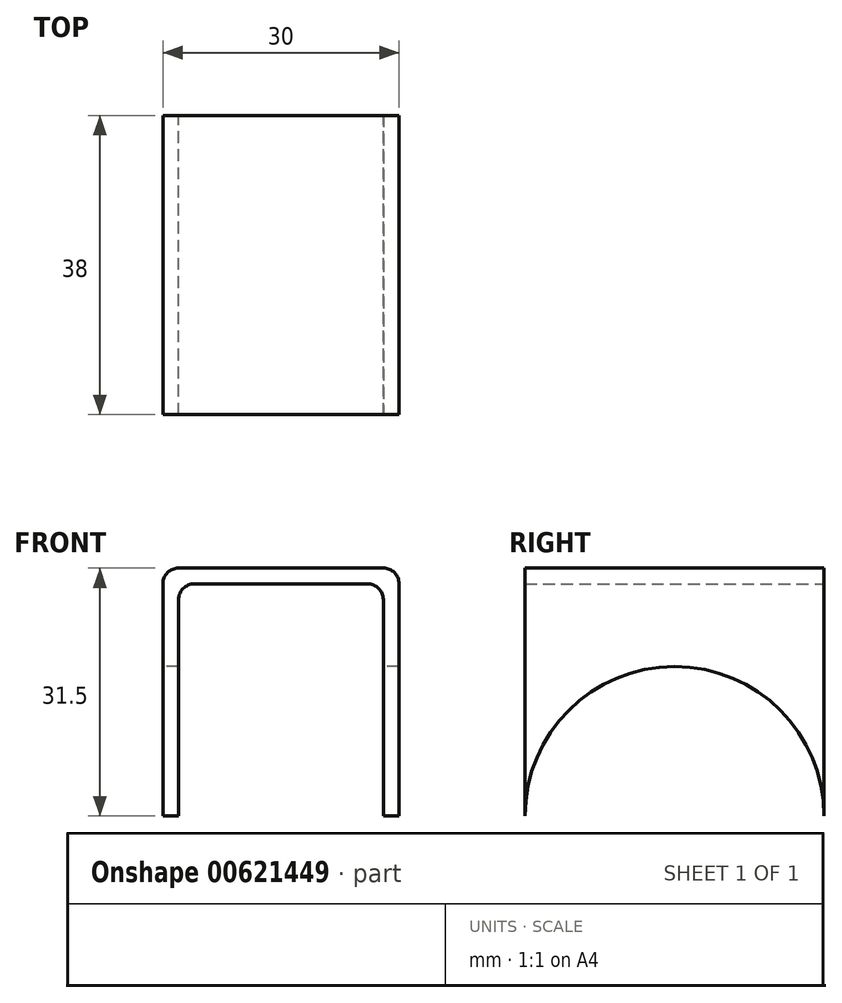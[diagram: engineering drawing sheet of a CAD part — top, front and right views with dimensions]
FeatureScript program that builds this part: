
annotation { "Feature Type Name" : "Feature", "Feature Type Description" : "" }
export const myFeature = defineFeature(function(context is Context, id is Id, definition is map)
    precondition{}
    {
        {
            var Q0;
            Q0=qCreatedBy(makeId("Front.planeOp"),FACE);
            var sketch = newSketch(context, id + "F0", { "sketchPlane" : qUnion([Q0])});
            skLineSegment(sketch, "E0", {"start": v(0, 0) * mm, "end": v(0, 29.5) * mm});
            skLineSegment(sketch, "E1", {"start": v(0, 29.5) * mm, "end": v(26, 29.5) * mm});
            skLineSegment(sketch, "E2", {"start": v(26, 29.5) * mm, "end": v(26, 0) * mm});
            skLineSegment(sketch, "E3", {"start": v(0, 0) * mm, "end": v(-2, 0) * mm});
            skLineSegment(sketch, "E4", {"start": v(-2, 0) * mm, "end": v(-2, 31.5) * mm});
            skLineSegment(sketch, "E5", {"start": v(-2, 31.5) * mm, "end": v(28, 31.5) * mm});
            skLineSegment(sketch, "E6", {"start": v(28, 31.5) * mm, "end": v(28, 0) * mm});
            skLineSegment(sketch, "E7", {"start": v(28, 0) * mm, "end": v(26, 0) * mm});
            skSolve(sketch);
        }
        {
            var Q0;
            Q0=makeQuery(id+"F0.imprint","IMPRINT",FACE,{"disambiguationData":[TD([[makeQuery(id+"F0.imprint","IMPRINT",EDGE,{"derivedFrom":sQuery(id+"F0.wireOp",EDGE,"E0")}),1.0]])]});
            extrude(context, id + "F1", {"entities" : qUnion([Q0]), "depth" : 38 * mm, "offsetDistance" : 25 * mm});
        }
        {
            var Q0;
            Q0=makeQuery(id+"F1.opExtrude","SWEPT_FACE",FACE,{"disambiguationData":[OSD([sQuery(id+"F0.wireOp",EDGE,"E4")])]});
            var sketch = newSketch(context, id + "F2", { "sketchPlane" : qUnion([Q0])});
            skCircle(sketch, "E8", {"center": v(19, 0) * mm, "radius": 19 * mm});
            skSolve(sketch);
        }
        {
            var Q0;
            {var subQ1=sQuery(id+"F0.wireOp",EDGE,"E4");var subQ2=makeQuery(id+"F1.opExtrude","SWEPT_EDGE",EDGE,{"disambiguationData":[OSD([sQuery(id+"F0.wireOp",EDGE,"E3"),subQ1])]});Q0=makeQuery(id+"F2.imprint","IMPRINT",FACE,{"disambiguationData":[TD([[makeQuery(id+"F2.imprint","IMPRINT",EDGE,{"derivedFrom":subQ2}),-1.0]])]});}
            var Q1;
            {var subQ1=sQuery(id+"F0.wireOp",EDGE,"E4");var subQ2=makeQuery(id+"F1.opExtrude","SWEPT_EDGE",EDGE,{"disambiguationData":[OSD([sQuery(id+"F0.wireOp",EDGE,"E3"),subQ1])]});Q1=makeQuery(id+"F2.imprint","IMPRINT",FACE,{"disambiguationData":[TD([[makeQuery(id+"F2.imprint","IMPRINT",EDGE,{"derivedFrom":subQ2}),1.0]])]});}
            extrude(context, id + "F3", {"entities" : qUnion([Q0, Q1]), "operationType" : NewBodyOperationType.REMOVE, "endBound" : BoundingType.THROUGH_ALL, "oppositeDirection" : true, "depth" : 25 * mm, "offsetDistance" : 25 * mm});
        }
        {
            var Q0;
            Q0=makeQuery(id+"F1.opExtrude","SWEPT_EDGE",EDGE,{"disambiguationData":[OSD([sQuery(id+"F0.wireOp",EDGE,"E1"),sQuery(id+"F0.wireOp",EDGE,"E2")])]});
            var Q1;
            Q1=makeQuery(id+"F1.opExtrude","SWEPT_EDGE",EDGE,{"disambiguationData":[OSD([sQuery(id+"F0.wireOp",EDGE,"E0"),sQuery(id+"F0.wireOp",EDGE,"E1")])]});
            var Q2;
            Q2=makeQuery(id+"F1.opExtrude","SWEPT_EDGE",EDGE,{"disambiguationData":[OSD([sQuery(id+"F0.wireOp",EDGE,"E5"),sQuery(id+"F0.wireOp",EDGE,"E6")])]});
            var Q3;
            Q3=makeQuery(id+"F1.opExtrude","SWEPT_EDGE",EDGE,{"disambiguationData":[OSD([sQuery(id+"F0.wireOp",EDGE,"E4"),sQuery(id+"F0.wireOp",EDGE,"E5")])]});
            fillet(context, id + "F4", {"entities" : qUnion([Q0, Q1, Q2, Q3]), "radius" : 2 * mm, "tangentPropagation" : true, "allowEdgeOverflow" : false});
        }
    });
